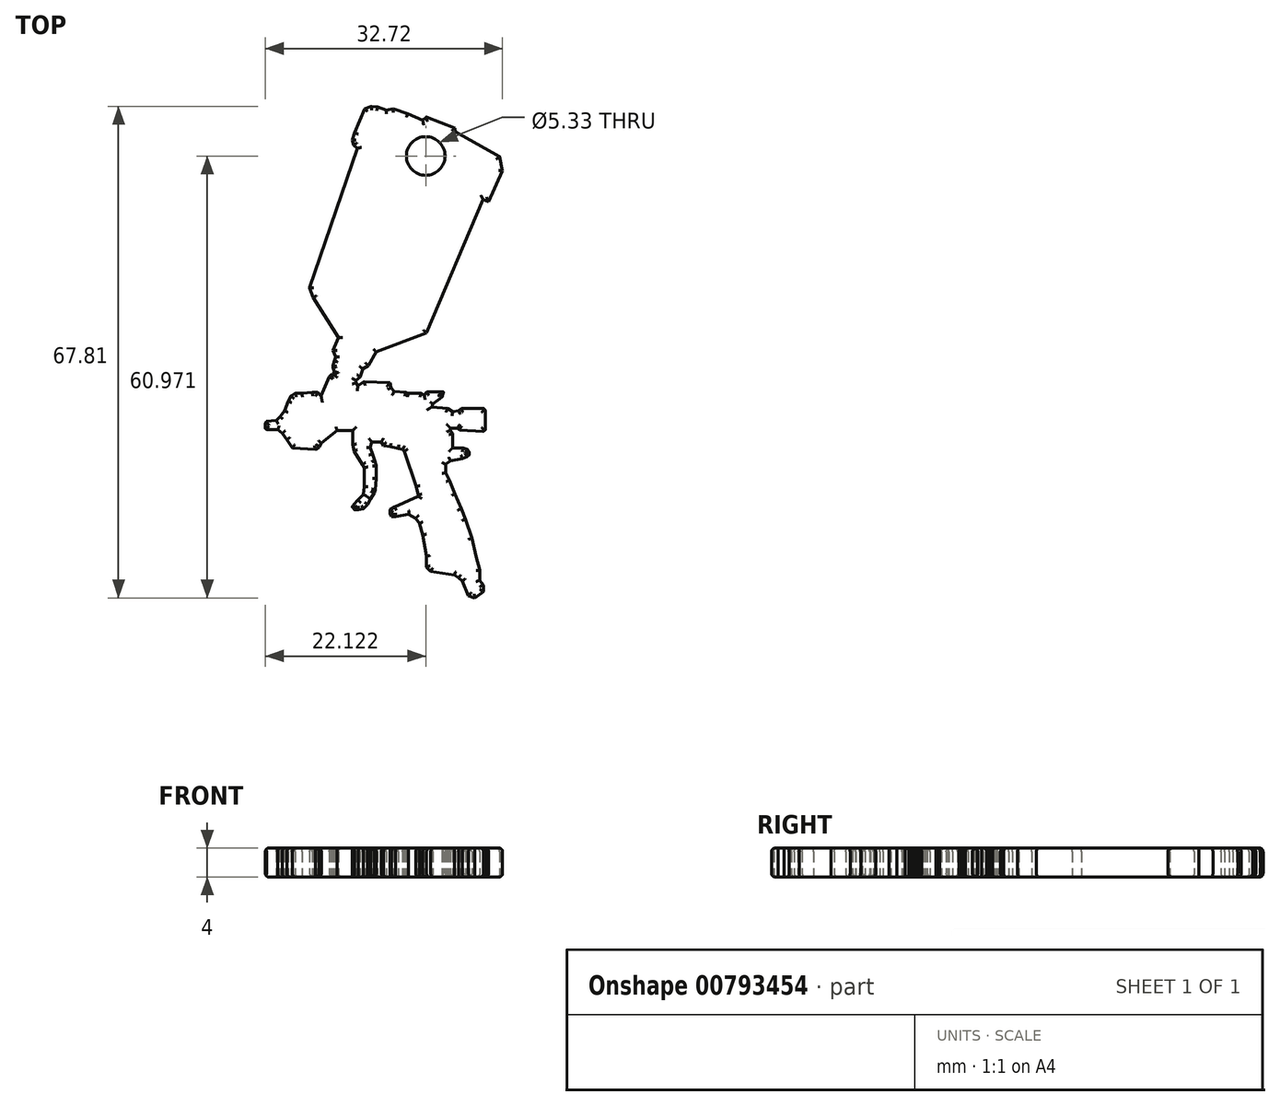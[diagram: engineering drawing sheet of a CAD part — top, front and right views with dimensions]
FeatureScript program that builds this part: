
annotation { "Feature Type Name" : "Feature", "Feature Type Description" : "" }
export const myFeature = defineFeature(function(context is Context, id is Id, definition is map)
    precondition{}
    {
        {
            var Q0;
            Q0=qCreatedBy(makeId("Top.planeOp"),FACE);
            var sketch = newSketch(context, id + "F0", { "sketchPlane" : qUnion([Q0])});
            skLineSegment(sketch, "E0", {"start": v(9.1, -28.8) * mm, "end": v(8.24, -26.79) * mm});
            skLineSegment(sketch, "E1", {"start": v(8.24, -26.79) * mm, "end": v(7.71, -26.36) * mm});
            skLineSegment(sketch, "E2", {"start": v(7.71, -26.36) * mm, "end": v(7.14, -25.97) * mm});
            skLineSegment(sketch, "E3", {"start": v(7.14, -25.97) * mm, "end": v(3.9, -25.45) * mm});
            skLineSegment(sketch, "E4", {"start": v(3.9, -25.45) * mm, "end": v(3.32, -24.88) * mm});
            skLineSegment(sketch, "E5", {"start": v(3.32, -24.88) * mm, "end": v(3.32, -23.3) * mm});
            skLineSegment(sketch, "E6", {"start": v(3.32, -23.3) * mm, "end": v(2.8, -20.43) * mm});
            skLineSegment(sketch, "E7", {"start": v(2.8, -20.43) * mm, "end": v(2.31, -18.85) * mm});
            skLineSegment(sketch, "E8", {"start": v(2.31, -18.85) * mm, "end": v(1.83, -18.13) * mm});
            skLineSegment(sketch, "E9", {"start": v(1.83, -18.13) * mm, "end": v(0.83, -17.56) * mm});
            skLineSegment(sketch, "E10", {"start": v(0.83, -17.56) * mm, "end": v(-0.93, -17.88) * mm});
            skLineSegment(sketch, "E11", {"start": v(-0.93, -17.88) * mm, "end": v(-1.5, -17.88) * mm});
            skLineSegment(sketch, "E12", {"start": v(-1.5, -17.88) * mm, "end": v(-1.75, -17.5) * mm});
            skLineSegment(sketch, "E13", {"start": v(-1.75, -17.5) * mm, "end": v(-1.75, -16.95) * mm});
            skLineSegment(sketch, "E14", {"start": v(-1.75, -16.95) * mm, "end": v(-1.07, -16.57) * mm});
            skLineSegment(sketch, "E15", {"start": v(-1.07, -16.57) * mm, "end": v(2.14, -15.08) * mm});
            skLineSegment(sketch, "E16", {"start": v(2.14, -15.08) * mm, "end": v(2.14, -14.85) * mm});
            skLineSegment(sketch, "E17", {"start": v(2.14, -14.85) * mm, "end": v(1.92, -13.74) * mm});
            skLineSegment(sketch, "E18", {"start": v(1.92, -13.74) * mm, "end": v(0.26, -8.88) * mm});
            skLineSegment(sketch, "E19", {"start": v(0.26, -8.88) * mm, "end": v(0, -8.63) * mm});
            skLineSegment(sketch, "E20", {"start": v(0, -8.63) * mm, "end": v(-0.6, -8.48) * mm});
            skLineSegment(sketch, "E21", {"start": v(-0.6, -8.48) * mm, "end": v(-1.68, -8.26) * mm});
            skLineSegment(sketch, "E22", {"start": v(-1.68, -8.26) * mm, "end": v(-2.6, -8.1) * mm});
            skLineSegment(sketch, "E23", {"start": v(-2.6, -8.1) * mm, "end": v(-2.92, -7.6) * mm});
            skLineSegment(sketch, "E24", {"start": v(-2.92, -7.6) * mm, "end": v(-4.24, -7.6) * mm});
            skLineSegment(sketch, "E25", {"start": v(-4.24, -7.6) * mm, "end": v(-4.43, -8.36) * mm});
            skLineSegment(sketch, "E26", {"start": v(-4.43, -8.36) * mm, "end": v(-4.14, -9.23) * mm});
            skLineSegment(sketch, "E27", {"start": v(-4.14, -9.23) * mm, "end": v(-3.79, -10.18) * mm});
            skLineSegment(sketch, "E28", {"start": v(-3.79, -10.18) * mm, "end": v(-3.65, -10.87) * mm});
            skLineSegment(sketch, "E29", {"start": v(-3.65, -10.87) * mm, "end": v(-3.65, -12.63) * mm});
            skLineSegment(sketch, "E30", {"start": v(-3.65, -12.63) * mm, "end": v(-3.78, -14.18) * mm});
            skLineSegment(sketch, "E31", {"start": v(-3.78, -14.18) * mm, "end": v(-3.9, -14.6) * mm});
            skLineSegment(sketch, "E32", {"start": v(-3.9, -14.6) * mm, "end": v(-4.38, -15.44) * mm});
            skLineSegment(sketch, "E33", {"start": v(-4.38, -15.44) * mm, "end": v(-4.81, -16.21) * mm});
            skLineSegment(sketch, "E34", {"start": v(-4.81, -16.21) * mm, "end": v(-5.4, -16.82) * mm});
            skLineSegment(sketch, "E35", {"start": v(-5.4, -16.82) * mm, "end": v(-6.07, -16.95) * mm});
            skLineSegment(sketch, "E36", {"start": v(-6.07, -16.95) * mm, "end": v(-6.62, -16.95) * mm});
            skLineSegment(sketch, "E37", {"start": v(-6.62, -16.95) * mm, "end": v(-6.94, -16.57) * mm});
            skLineSegment(sketch, "E38", {"start": v(-6.94, -16.57) * mm, "end": v(-6.74, -16.21) * mm});
            skLineSegment(sketch, "E39", {"start": v(-6.74, -16.21) * mm, "end": v(-6.14, -15.6) * mm});
            skLineSegment(sketch, "E40", {"start": v(-6.14, -15.6) * mm, "end": v(-5.38, -14.85) * mm});
            skLineSegment(sketch, "E41", {"start": v(-5.38, -14.85) * mm, "end": v(-5.26, -13.74) * mm});
            skLineSegment(sketch, "E42", {"start": v(-5.26, -13.74) * mm, "end": v(-5.26, -12.38) * mm});
            skLineSegment(sketch, "E43", {"start": v(-5.26, -12.38) * mm, "end": v(-5.26, -11.15) * mm});
            skLineSegment(sketch, "E44", {"start": v(-5.26, -11.15) * mm, "end": v(-5.5, -10.69) * mm});
            skLineSegment(sketch, "E45", {"start": v(-5.5, -10.69) * mm, "end": v(-6.7, -8.85) * mm});
            skLineSegment(sketch, "E46", {"start": v(-6.7, -8.85) * mm, "end": v(-6.87, -7.93) * mm});
            skLineSegment(sketch, "E47", {"start": v(-6.87, -7.93) * mm, "end": v(-6.87, -6.03) * mm});
            skLineSegment(sketch, "E48", {"start": v(-6.87, -6.03) * mm, "end": v(-9, -6.03) * mm});
            skLineSegment(sketch, "E49", {"start": v(-9, -6.03) * mm, "end": v(-11.2, -7.74) * mm});
            skLineSegment(sketch, "E50", {"start": v(-11.2, -7.74) * mm, "end": v(-11.5, -8.29) * mm});
            skLineSegment(sketch, "E51", {"start": v(-11.5, -8.29) * mm, "end": v(-12.01, -8.63) * mm});
            skLineSegment(sketch, "E52", {"start": v(-12.01, -8.63) * mm, "end": v(-15.17, -8.45) * mm});
            skLineSegment(sketch, "E53", {"start": v(-15.17, -8.45) * mm, "end": v(-15.95, -7.27) * mm});
            skLineSegment(sketch, "E54", {"start": v(-15.95, -7.27) * mm, "end": v(-16.58, -6.4) * mm});
            skLineSegment(sketch, "E55", {"start": v(-16.58, -6.4) * mm, "end": v(-17.2, -5.88) * mm});
            skLineSegment(sketch, "E56", {"start": v(-17.2, -5.88) * mm, "end": v(-18.72, -5.88) * mm});
            skLineSegment(sketch, "E57", {"start": v(-18.72, -5.88) * mm, "end": v(-18.92, -5.77) * mm});
            skLineSegment(sketch, "E58", {"start": v(-18.92, -5.77) * mm, "end": v(-18.92, -5.02) * mm});
            skLineSegment(sketch, "E59", {"start": v(-18.92, -5.02) * mm, "end": v(-18.78, -4.77) * mm});
            skLineSegment(sketch, "E60", {"start": v(-18.78, -4.77) * mm, "end": v(-17.4, -4.62) * mm});
            skLineSegment(sketch, "E61", {"start": v(-17.4, -4.62) * mm, "end": v(-16.88, -4.11) * mm});
            skLineSegment(sketch, "E62", {"start": v(-16.88, -4.11) * mm, "end": v(-16.3, -3.27) * mm});
            skLineSegment(sketch, "E63", {"start": v(-16.3, -3.27) * mm, "end": v(-15.78, -1.95) * mm});
            skLineSegment(sketch, "E64", {"start": v(-15.78, -1.95) * mm, "end": v(-15.38, -1.22) * mm});
            skLineSegment(sketch, "E65", {"start": v(-15.38, -1.22) * mm, "end": v(-14.79, -0.87) * mm});
            skLineSegment(sketch, "E66", {"start": v(-14.79, -0.87) * mm, "end": v(-13.83, -0.87) * mm});
            skLineSegment(sketch, "E67", {"start": v(-13.83, -0.87) * mm, "end": v(-12.43, -0.75) * mm});
            skLineSegment(sketch, "E68", {"start": v(-12.43, -0.75) * mm, "end": v(-11.72, -0.75) * mm});
            skLineSegment(sketch, "E69", {"start": v(-11.72, -0.75) * mm, "end": v(-11.23, -1.26) * mm});
            skLineSegment(sketch, "E70", {"start": v(-11.23, -1.26) * mm, "end": v(-10.1, 1.4) * mm});
            skLineSegment(sketch, "E71", {"start": v(-10.1, 1.4) * mm, "end": v(-9.85, 1.65) * mm});
            skLineSegment(sketch, "E72", {"start": v(-9.85, 1.65) * mm, "end": v(-9.56, 1.7) * mm});
            skLineSegment(sketch, "E73", {"start": v(-9.56, 1.7) * mm, "end": v(-9.6, 1.88) * mm});
            skLineSegment(sketch, "E74", {"start": v(-9.6, 1.88) * mm, "end": v(-9.39, 2.08) * mm});
            skLineSegment(sketch, "E75", {"start": v(-9.39, 2.08) * mm, "end": v(-9.61, 2.7) * mm});
            skLineSegment(sketch, "E76", {"start": v(-9.61, 2.7) * mm, "end": v(-9.61, 2.93) * mm});
            skLineSegment(sketch, "E77", {"start": v(-9.61, 2.93) * mm, "end": v(-9.4, 3.6) * mm});
            skLineSegment(sketch, "E78", {"start": v(-9.4, 3.6) * mm, "end": v(-9.23, 4.13) * mm});
            skLineSegment(sketch, "E79", {"start": v(-9.23, 4.13) * mm, "end": v(-9.56, 5.02) * mm});
            skLineSegment(sketch, "E80", {"start": v(-9.56, 5.02) * mm, "end": v(-8.84, 6.8) * mm});
            skLineSegment(sketch, "E81", {"start": v(-8.84, 6.8) * mm, "end": v(-12.32, 12.35) * mm});
            skLineSegment(sketch, "E82", {"start": v(-12.32, 12.35) * mm, "end": v(-12.8, 13.65) * mm});
            skLineSegment(sketch, "E83", {"start": v(-12.8, 13.65) * mm, "end": v(-6.26, 32.91) * mm});
            skLineSegment(sketch, "E84", {"start": v(-6.26, 32.91) * mm, "end": v(-6.7, 33.38) * mm});
            skLineSegment(sketch, "E85", {"start": v(-6.7, 33.38) * mm, "end": v(-6.94, 34.03) * mm});
            skLineSegment(sketch, "E86", {"start": v(-6.94, 34.03) * mm, "end": v(-6.6, 35.06) * mm});
            skLineSegment(sketch, "E87", {"start": v(-6.6, 35.06) * mm, "end": v(-5.2, 38.37) * mm});
            skLineSegment(sketch, "E88", {"start": v(-5.2, 38.37) * mm, "end": v(-4.32, 38.7) * mm});
            skLineSegment(sketch, "E89", {"start": v(-4.32, 38.7) * mm, "end": v(-3.45, 38.6) * mm});
            skLineSegment(sketch, "E90", {"start": v(-3.45, 38.6) * mm, "end": v(-2.2, 38.18) * mm});
            skLineSegment(sketch, "E91", {"start": v(-2.2, 38.18) * mm, "end": v(-1.25, 38.36) * mm});
            skLineSegment(sketch, "E92", {"start": v(-1.25, 38.36) * mm, "end": v(0.73, 37.69) * mm});
            skLineSegment(sketch, "E93", {"start": v(0.73, 37.69) * mm, "end": v(2.8, 36.77) * mm});
            skLineSegment(sketch, "E94", {"start": v(2.8, 36.77) * mm, "end": v(3.29, 37.25) * mm});
            skLineSegment(sketch, "E95", {"start": v(3.29, 37.25) * mm, "end": v(7.21, 35.67) * mm});
            skLineSegment(sketch, "E96", {"start": v(7.21, 35.67) * mm, "end": v(7.3, 35.2) * mm});
            skLineSegment(sketch, "E97", {"start": v(7.3, 35.2) * mm, "end": v(13.42, 31.78) * mm});
            skLineSegment(sketch, "E98", {"start": v(13.42, 31.78) * mm, "end": v(13.8, 29.8) * mm});
            skLineSegment(sketch, "E99", {"start": v(13.8, 29.8) * mm, "end": v(11.86, 25.58) * mm});
            skLineSegment(sketch, "E100", {"start": v(11.86, 25.58) * mm, "end": v(11.1, 25.83) * mm});
            skLineSegment(sketch, "E101", {"start": v(11.1, 25.83) * mm, "end": v(3.29, 7.42) * mm});
            skLineSegment(sketch, "E102", {"start": v(3.29, 7.42) * mm, "end": v(-1.5, 5.63) * mm});
            skLineSegment(sketch, "E103", {"start": v(-1.5, 5.63) * mm, "end": v(-3.65, 4.82) * mm});
            skLineSegment(sketch, "E104", {"start": v(-3.65, 4.82) * mm, "end": v(-4.71, 2.93) * mm});
            skLineSegment(sketch, "E105", {"start": v(-4.71, 2.93) * mm, "end": v(-5.5, 2.5) * mm});
            skLineSegment(sketch, "E106", {"start": v(-5.5, 2.5) * mm, "end": v(-5.83, 1.38) * mm});
            skLineSegment(sketch, "E107", {"start": v(-5.83, 1.38) * mm, "end": v(-6.44, 0.93) * mm});
            skLineSegment(sketch, "E108", {"start": v(-6.44, 0.93) * mm, "end": v(-6.44, 0.56) * mm});
            skLineSegment(sketch, "E109", {"start": v(-6.44, 0.56) * mm, "end": v(-6.15, 0.15) * mm});
            skLineSegment(sketch, "E110", {"start": v(-6.15, 0.15) * mm, "end": v(-5.32, 0.75) * mm});
            skLineSegment(sketch, "E111", {"start": v(-5.32, 0.75) * mm, "end": v(-1.74, 0.56) * mm});
            skLineSegment(sketch, "E112", {"start": v(-1.74, 0.56) * mm, "end": v(-1.58, -0.12) * mm});
            skLineSegment(sketch, "E113", {"start": v(-1.58, -0.12) * mm, "end": v(-1.17, -0.65) * mm});
            skLineSegment(sketch, "E114", {"start": v(-1.17, -0.65) * mm, "end": v(0.41, -0.77) * mm});
            skLineSegment(sketch, "E115", {"start": v(0.41, -0.77) * mm, "end": v(0.77, -0.86) * mm});
            skLineSegment(sketch, "E116", {"start": v(0.77, -0.86) * mm, "end": v(2.55, -0.86) * mm});
            skLineSegment(sketch, "E117", {"start": v(2.55, -0.86) * mm, "end": v(3, -1.11) * mm});
            skLineSegment(sketch, "E118", {"start": v(3, -1.11) * mm, "end": v(3.39, -0.7) * mm});
            skLineSegment(sketch, "E119", {"start": v(3.39, -0.7) * mm, "end": v(5.67, -0.7) * mm});
            skLineSegment(sketch, "E120", {"start": v(5.67, -0.7) * mm, "end": v(5.46, -1.4) * mm});
            skLineSegment(sketch, "E121", {"start": v(5.46, -1.4) * mm, "end": v(4.9, -1.83) * mm});
            skLineSegment(sketch, "E122", {"start": v(4.9, -1.83) * mm, "end": v(4.2, -2.36) * mm});
            skLineSegment(sketch, "E123", {"start": v(4.2, -2.36) * mm, "end": v(4.05, -2.76) * mm});
            skLineSegment(sketch, "E124", {"start": v(4.05, -2.76) * mm, "end": v(6.2, -2.96) * mm});
            skLineSegment(sketch, "E125", {"start": v(6.2, -2.96) * mm, "end": v(6.92, -3.44) * mm});
            skLineSegment(sketch, "E126", {"start": v(6.92, -3.44) * mm, "end": v(7.73, -3.28) * mm});
            skLineSegment(sketch, "E127", {"start": v(7.73, -3.28) * mm, "end": v(8.12, -2.98) * mm});
            skLineSegment(sketch, "E128", {"start": v(8.12, -2.98) * mm, "end": v(11.23, -2.98) * mm});
            skLineSegment(sketch, "E129", {"start": v(11.23, -2.98) * mm, "end": v(11.44, -3.27) * mm});
            skLineSegment(sketch, "E130", {"start": v(11.44, -3.27) * mm, "end": v(11.44, -5.91) * mm});
            skLineSegment(sketch, "E131", {"start": v(11.44, -5.91) * mm, "end": v(11.14, -6.14) * mm});
            skLineSegment(sketch, "E132", {"start": v(11.14, -6.14) * mm, "end": v(7.85, -5.95) * mm});
            skLineSegment(sketch, "E133", {"start": v(7.85, -5.95) * mm, "end": v(7.64, -5.68) * mm});
            skLineSegment(sketch, "E134", {"start": v(7.64, -5.68) * mm, "end": v(6.6, -5.68) * mm});
            skLineSegment(sketch, "E135", {"start": v(6.6, -5.68) * mm, "end": v(6.6, -6.01) * mm});
            skLineSegment(sketch, "E136", {"start": v(6.6, -6.01) * mm, "end": v(6.91, -6.42) * mm});
            skLineSegment(sketch, "E137", {"start": v(6.91, -6.42) * mm, "end": v(6.91, -8.4) * mm});
            skLineSegment(sketch, "E138", {"start": v(6.91, -8.4) * mm, "end": v(8.35, -8.4) * mm});
            skLineSegment(sketch, "E139", {"start": v(8.35, -8.4) * mm, "end": v(8.94, -8.62) * mm});
            skLineSegment(sketch, "E140", {"start": v(8.94, -8.62) * mm, "end": v(9.21, -8.98) * mm});
            skLineSegment(sketch, "E141", {"start": v(9.21, -8.98) * mm, "end": v(9.21, -9.35) * mm});
            skLineSegment(sketch, "E142", {"start": v(9.21, -9.35) * mm, "end": v(8.88, -9.6) * mm});
            skLineSegment(sketch, "E143", {"start": v(8.88, -9.6) * mm, "end": v(8.23, -9.87) * mm});
            skLineSegment(sketch, "E144", {"start": v(8.23, -9.87) * mm, "end": v(6.6, -10.2) * mm});
            skLineSegment(sketch, "E145", {"start": v(6.6, -10.2) * mm, "end": v(5.97, -10.67) * mm});
            skLineSegment(sketch, "E146", {"start": v(5.97, -10.67) * mm, "end": v(5.97, -11.26) * mm});
            skLineSegment(sketch, "E147", {"start": v(5.97, -11.26) * mm, "end": v(5.97, -11.83) * mm});
            skLineSegment(sketch, "E148", {"start": v(5.97, -11.83) * mm, "end": v(6.47, -12.87) * mm});
            skLineSegment(sketch, "E149", {"start": v(6.47, -12.87) * mm, "end": v(7.23, -14.77) * mm});
            skLineSegment(sketch, "E150", {"start": v(7.23, -14.77) * mm, "end": v(8.1, -16.8) * mm});
            skLineSegment(sketch, "E151", {"start": v(8.1, -16.8) * mm, "end": v(8.66, -18.26) * mm});
            skLineSegment(sketch, "E152", {"start": v(8.66, -18.26) * mm, "end": v(9.55, -20.9) * mm});
            skLineSegment(sketch, "E153", {"start": v(9.55, -20.9) * mm, "end": v(10.18, -23.41) * mm});
            skLineSegment(sketch, "E154", {"start": v(10.18, -23.41) * mm, "end": v(10.65, -25.27) * mm});
            skLineSegment(sketch, "E155", {"start": v(10.65, -25.27) * mm, "end": v(10.65, -26.16) * mm});
            skLineSegment(sketch, "E156", {"start": v(10.65, -26.16) * mm, "end": v(10.65, -26.69) * mm});
            skLineSegment(sketch, "E157", {"start": v(10.65, -26.69) * mm, "end": v(11.16, -27.35) * mm});
            skLineSegment(sketch, "E158", {"start": v(11.16, -27.35) * mm, "end": v(11.16, -28.21) * mm});
            skLineSegment(sketch, "E159", {"start": v(11.16, -28.21) * mm, "end": v(10.6, -28.65) * mm});
            skLineSegment(sketch, "E160", {"start": v(10.6, -28.65) * mm, "end": v(9.99, -29.11) * mm});
            skLineSegment(sketch, "E161", {"start": v(9.99, -29.11) * mm, "end": v(9.1, -28.8) * mm});
            skCircle(sketch, "E162", {"center": v(3.2, 31.86) * mm, "radius": 2.67 * mm});
            skSolve(sketch);
        }
        {
            var Q0;
            Q0 = qSketchRegion(id + "F0", true);
            var Q1;
            Q1=makeQuery(id+"F0.imprint","IMPRINT",FACE,{"disambiguationData":[TD([[makeQuery(id+"F0.imprint","IMPRINT",EDGE,{"derivedFrom":sQuery(id+"F0.wireOp",EDGE,"E0")}),-1.0]])]});
            extrude(context, id + "F1", {"entities" : qUnion([Q0, Q1]), "depth" : 4 * mm, "offsetDistance" : 25 * mm});
        }
        {
            var Q0;
            Q0=makeQuery(id+"F1.opExtrude","CAP_FACE",FACE,{"disambiguationData":[OSD([sQuery(id+"F0.wireOp",EDGE,"E0"),sQuery(id+"F0.wireOp",EDGE,"E1"),sQuery(id+"F0.wireOp",EDGE,"E2"),sQuery(id+"F0.wireOp",EDGE,"E3"),sQuery(id+"F0.wireOp",EDGE,"E4"),sQuery(id+"F0.wireOp",EDGE,"E5"),sQuery(id+"F0.wireOp",EDGE,"E6"),sQuery(id+"F0.wireOp",EDGE,"E7"),sQuery(id+"F0.wireOp",EDGE,"E8"),sQuery(id+"F0.wireOp",EDGE,"E9"),sQuery(id+"F0.wireOp",EDGE,"E10"),sQuery(id+"F0.wireOp",EDGE,"E11"),sQuery(id+"F0.wireOp",EDGE,"E12"),sQuery(id+"F0.wireOp",EDGE,"E13"),sQuery(id+"F0.wireOp",EDGE,"E14"),sQuery(id+"F0.wireOp",EDGE,"E15"),sQuery(id+"F0.wireOp",EDGE,"E16"),sQuery(id+"F0.wireOp",EDGE,"E17"),sQuery(id+"F0.wireOp",EDGE,"E18"),sQuery(id+"F0.wireOp",EDGE,"E19"),sQuery(id+"F0.wireOp",EDGE,"E20"),sQuery(id+"F0.wireOp",EDGE,"E21"),sQuery(id+"F0.wireOp",EDGE,"E22"),sQuery(id+"F0.wireOp",EDGE,"E23"),sQuery(id+"F0.wireOp",EDGE,"E24"),sQuery(id+"F0.wireOp",EDGE,"E25"),sQuery(id+"F0.wireOp",EDGE,"E26"),sQuery(id+"F0.wireOp",EDGE,"E27"),sQuery(id+"F0.wireOp",EDGE,"E28"),sQuery(id+"F0.wireOp",EDGE,"E29"),sQuery(id+"F0.wireOp",EDGE,"E30"),sQuery(id+"F0.wireOp",EDGE,"E31"),sQuery(id+"F0.wireOp",EDGE,"E32"),sQuery(id+"F0.wireOp",EDGE,"E33"),sQuery(id+"F0.wireOp",EDGE,"E34"),sQuery(id+"F0.wireOp",EDGE,"E35"),sQuery(id+"F0.wireOp",EDGE,"E36"),sQuery(id+"F0.wireOp",EDGE,"E37"),sQuery(id+"F0.wireOp",EDGE,"E38"),sQuery(id+"F0.wireOp",EDGE,"E39"),sQuery(id+"F0.wireOp",EDGE,"E40"),sQuery(id+"F0.wireOp",EDGE,"E41"),sQuery(id+"F0.wireOp",EDGE,"E42"),sQuery(id+"F0.wireOp",EDGE,"E43"),sQuery(id+"F0.wireOp",EDGE,"E44"),sQuery(id+"F0.wireOp",EDGE,"E45"),sQuery(id+"F0.wireOp",EDGE,"E46"),sQuery(id+"F0.wireOp",EDGE,"E47"),sQuery(id+"F0.wireOp",EDGE,"E48"),sQuery(id+"F0.wireOp",EDGE,"E49"),sQuery(id+"F0.wireOp",EDGE,"E50"),sQuery(id+"F0.wireOp",EDGE,"E51"),sQuery(id+"F0.wireOp",EDGE,"E52"),sQuery(id+"F0.wireOp",EDGE,"E53"),sQuery(id+"F0.wireOp",EDGE,"E54"),sQuery(id+"F0.wireOp",EDGE,"E55"),sQuery(id+"F0.wireOp",EDGE,"E56"),sQuery(id+"F0.wireOp",EDGE,"E57"),sQuery(id+"F0.wireOp",EDGE,"E58"),sQuery(id+"F0.wireOp",EDGE,"E59"),sQuery(id+"F0.wireOp",EDGE,"E60"),sQuery(id+"F0.wireOp",EDGE,"E61"),sQuery(id+"F0.wireOp",EDGE,"E62"),sQuery(id+"F0.wireOp",EDGE,"E63"),sQuery(id+"F0.wireOp",EDGE,"E64"),sQuery(id+"F0.wireOp",EDGE,"E65"),sQuery(id+"F0.wireOp",EDGE,"E66"),sQuery(id+"F0.wireOp",EDGE,"E67"),sQuery(id+"F0.wireOp",EDGE,"E68"),sQuery(id+"F0.wireOp",EDGE,"E69"),sQuery(id+"F0.wireOp",EDGE,"E70"),sQuery(id+"F0.wireOp",EDGE,"E71"),sQuery(id+"F0.wireOp",EDGE,"E72"),sQuery(id+"F0.wireOp",EDGE,"E73"),sQuery(id+"F0.wireOp",EDGE,"E74"),sQuery(id+"F0.wireOp",EDGE,"E75"),sQuery(id+"F0.wireOp",EDGE,"E76"),sQuery(id+"F0.wireOp",EDGE,"E77"),sQuery(id+"F0.wireOp",EDGE,"E78"),sQuery(id+"F0.wireOp",EDGE,"E79"),sQuery(id+"F0.wireOp",EDGE,"E80"),sQuery(id+"F0.wireOp",EDGE,"E81"),sQuery(id+"F0.wireOp",EDGE,"E82"),sQuery(id+"F0.wireOp",EDGE,"E83"),sQuery(id+"F0.wireOp",EDGE,"E84"),sQuery(id+"F0.wireOp",EDGE,"E85"),sQuery(id+"F0.wireOp",EDGE,"E86"),sQuery(id+"F0.wireOp",EDGE,"E87"),sQuery(id+"F0.wireOp",EDGE,"E88"),sQuery(id+"F0.wireOp",EDGE,"E89"),sQuery(id+"F0.wireOp",EDGE,"E90"),sQuery(id+"F0.wireOp",EDGE,"E91"),sQuery(id+"F0.wireOp",EDGE,"E92"),sQuery(id+"F0.wireOp",EDGE,"E93"),sQuery(id+"F0.wireOp",EDGE,"E94"),sQuery(id+"F0.wireOp",EDGE,"E95"),sQuery(id+"F0.wireOp",EDGE,"E96"),sQuery(id+"F0.wireOp",EDGE,"E97"),sQuery(id+"F0.wireOp",EDGE,"E98"),sQuery(id+"F0.wireOp",EDGE,"E99"),sQuery(id+"F0.wireOp",EDGE,"E100"),sQuery(id+"F0.wireOp",EDGE,"E101"),sQuery(id+"F0.wireOp",EDGE,"E102"),sQuery(id+"F0.wireOp",EDGE,"E103"),sQuery(id+"F0.wireOp",EDGE,"E104"),sQuery(id+"F0.wireOp",EDGE,"E105"),sQuery(id+"F0.wireOp",EDGE,"E106"),sQuery(id+"F0.wireOp",EDGE,"E107"),sQuery(id+"F0.wireOp",EDGE,"E108"),sQuery(id+"F0.wireOp",EDGE,"E109"),sQuery(id+"F0.wireOp",EDGE,"E110"),sQuery(id+"F0.wireOp",EDGE,"E111"),sQuery(id+"F0.wireOp",EDGE,"E112"),sQuery(id+"F0.wireOp",EDGE,"E113"),sQuery(id+"F0.wireOp",EDGE,"E114"),sQuery(id+"F0.wireOp",EDGE,"E115"),sQuery(id+"F0.wireOp",EDGE,"E116"),sQuery(id+"F0.wireOp",EDGE,"E117"),sQuery(id+"F0.wireOp",EDGE,"E118"),sQuery(id+"F0.wireOp",EDGE,"E119"),sQuery(id+"F0.wireOp",EDGE,"E120"),sQuery(id+"F0.wireOp",EDGE,"E121"),sQuery(id+"F0.wireOp",EDGE,"E122"),sQuery(id+"F0.wireOp",EDGE,"E123"),sQuery(id+"F0.wireOp",EDGE,"E124"),sQuery(id+"F0.wireOp",EDGE,"E125"),sQuery(id+"F0.wireOp",EDGE,"E126"),sQuery(id+"F0.wireOp",EDGE,"E127"),sQuery(id+"F0.wireOp",EDGE,"E128"),sQuery(id+"F0.wireOp",EDGE,"E129"),sQuery(id+"F0.wireOp",EDGE,"E130"),sQuery(id+"F0.wireOp",EDGE,"E131"),sQuery(id+"F0.wireOp",EDGE,"E132"),sQuery(id+"F0.wireOp",EDGE,"E133"),sQuery(id+"F0.wireOp",EDGE,"E134"),sQuery(id+"F0.wireOp",EDGE,"E135"),sQuery(id+"F0.wireOp",EDGE,"E136"),sQuery(id+"F0.wireOp",EDGE,"E137"),sQuery(id+"F0.wireOp",EDGE,"E138"),sQuery(id+"F0.wireOp",EDGE,"E139"),sQuery(id+"F0.wireOp",EDGE,"E140"),sQuery(id+"F0.wireOp",EDGE,"E141"),sQuery(id+"F0.wireOp",EDGE,"E142"),sQuery(id+"F0.wireOp",EDGE,"E143"),sQuery(id+"F0.wireOp",EDGE,"E144"),sQuery(id+"F0.wireOp",EDGE,"E145"),sQuery(id+"F0.wireOp",EDGE,"E146"),sQuery(id+"F0.wireOp",EDGE,"E147"),sQuery(id+"F0.wireOp",EDGE,"E148"),sQuery(id+"F0.wireOp",EDGE,"E149"),sQuery(id+"F0.wireOp",EDGE,"E150"),sQuery(id+"F0.wireOp",EDGE,"E151"),sQuery(id+"F0.wireOp",EDGE,"E152"),sQuery(id+"F0.wireOp",EDGE,"E153"),sQuery(id+"F0.wireOp",EDGE,"E154"),sQuery(id+"F0.wireOp",EDGE,"E155"),sQuery(id+"F0.wireOp",EDGE,"E156"),sQuery(id+"F0.wireOp",EDGE,"E157"),sQuery(id+"F0.wireOp",EDGE,"E158"),sQuery(id+"F0.wireOp",EDGE,"E159"),sQuery(id+"F0.wireOp",EDGE,"E160"),sQuery(id+"F0.wireOp",EDGE,"E161"),sQuery(id+"F0.wireOp",EDGE,"E162")])],"isStart":false});
            var Q1;
            Q1=makeQuery(id+"F1.opExtrude","CAP_FACE",FACE,{"disambiguationData":[OSD([sQuery(id+"F0.wireOp",EDGE,"E0"),sQuery(id+"F0.wireOp",EDGE,"E1"),sQuery(id+"F0.wireOp",EDGE,"E2"),sQuery(id+"F0.wireOp",EDGE,"E3"),sQuery(id+"F0.wireOp",EDGE,"E4"),sQuery(id+"F0.wireOp",EDGE,"E5"),sQuery(id+"F0.wireOp",EDGE,"E6"),sQuery(id+"F0.wireOp",EDGE,"E7"),sQuery(id+"F0.wireOp",EDGE,"E8"),sQuery(id+"F0.wireOp",EDGE,"E9"),sQuery(id+"F0.wireOp",EDGE,"E10"),sQuery(id+"F0.wireOp",EDGE,"E11"),sQuery(id+"F0.wireOp",EDGE,"E12"),sQuery(id+"F0.wireOp",EDGE,"E13"),sQuery(id+"F0.wireOp",EDGE,"E14"),sQuery(id+"F0.wireOp",EDGE,"E15"),sQuery(id+"F0.wireOp",EDGE,"E16"),sQuery(id+"F0.wireOp",EDGE,"E17"),sQuery(id+"F0.wireOp",EDGE,"E18"),sQuery(id+"F0.wireOp",EDGE,"E19"),sQuery(id+"F0.wireOp",EDGE,"E20"),sQuery(id+"F0.wireOp",EDGE,"E21"),sQuery(id+"F0.wireOp",EDGE,"E22"),sQuery(id+"F0.wireOp",EDGE,"E23"),sQuery(id+"F0.wireOp",EDGE,"E24"),sQuery(id+"F0.wireOp",EDGE,"E25"),sQuery(id+"F0.wireOp",EDGE,"E26"),sQuery(id+"F0.wireOp",EDGE,"E27"),sQuery(id+"F0.wireOp",EDGE,"E28"),sQuery(id+"F0.wireOp",EDGE,"E29"),sQuery(id+"F0.wireOp",EDGE,"E30"),sQuery(id+"F0.wireOp",EDGE,"E31"),sQuery(id+"F0.wireOp",EDGE,"E32"),sQuery(id+"F0.wireOp",EDGE,"E33"),sQuery(id+"F0.wireOp",EDGE,"E34"),sQuery(id+"F0.wireOp",EDGE,"E35"),sQuery(id+"F0.wireOp",EDGE,"E36"),sQuery(id+"F0.wireOp",EDGE,"E37"),sQuery(id+"F0.wireOp",EDGE,"E38"),sQuery(id+"F0.wireOp",EDGE,"E39"),sQuery(id+"F0.wireOp",EDGE,"E40"),sQuery(id+"F0.wireOp",EDGE,"E41"),sQuery(id+"F0.wireOp",EDGE,"E42"),sQuery(id+"F0.wireOp",EDGE,"E43"),sQuery(id+"F0.wireOp",EDGE,"E44"),sQuery(id+"F0.wireOp",EDGE,"E45"),sQuery(id+"F0.wireOp",EDGE,"E46"),sQuery(id+"F0.wireOp",EDGE,"E47"),sQuery(id+"F0.wireOp",EDGE,"E48"),sQuery(id+"F0.wireOp",EDGE,"E49"),sQuery(id+"F0.wireOp",EDGE,"E50"),sQuery(id+"F0.wireOp",EDGE,"E51"),sQuery(id+"F0.wireOp",EDGE,"E52"),sQuery(id+"F0.wireOp",EDGE,"E53"),sQuery(id+"F0.wireOp",EDGE,"E54"),sQuery(id+"F0.wireOp",EDGE,"E55"),sQuery(id+"F0.wireOp",EDGE,"E56"),sQuery(id+"F0.wireOp",EDGE,"E57"),sQuery(id+"F0.wireOp",EDGE,"E58"),sQuery(id+"F0.wireOp",EDGE,"E59"),sQuery(id+"F0.wireOp",EDGE,"E60"),sQuery(id+"F0.wireOp",EDGE,"E61"),sQuery(id+"F0.wireOp",EDGE,"E62"),sQuery(id+"F0.wireOp",EDGE,"E63"),sQuery(id+"F0.wireOp",EDGE,"E64"),sQuery(id+"F0.wireOp",EDGE,"E65"),sQuery(id+"F0.wireOp",EDGE,"E66"),sQuery(id+"F0.wireOp",EDGE,"E67"),sQuery(id+"F0.wireOp",EDGE,"E68"),sQuery(id+"F0.wireOp",EDGE,"E69"),sQuery(id+"F0.wireOp",EDGE,"E70"),sQuery(id+"F0.wireOp",EDGE,"E71"),sQuery(id+"F0.wireOp",EDGE,"E72"),sQuery(id+"F0.wireOp",EDGE,"E73"),sQuery(id+"F0.wireOp",EDGE,"E74"),sQuery(id+"F0.wireOp",EDGE,"E75"),sQuery(id+"F0.wireOp",EDGE,"E76"),sQuery(id+"F0.wireOp",EDGE,"E77"),sQuery(id+"F0.wireOp",EDGE,"E78"),sQuery(id+"F0.wireOp",EDGE,"E79"),sQuery(id+"F0.wireOp",EDGE,"E80"),sQuery(id+"F0.wireOp",EDGE,"E81"),sQuery(id+"F0.wireOp",EDGE,"E82"),sQuery(id+"F0.wireOp",EDGE,"E83"),sQuery(id+"F0.wireOp",EDGE,"E84"),sQuery(id+"F0.wireOp",EDGE,"E85"),sQuery(id+"F0.wireOp",EDGE,"E86"),sQuery(id+"F0.wireOp",EDGE,"E87"),sQuery(id+"F0.wireOp",EDGE,"E88"),sQuery(id+"F0.wireOp",EDGE,"E89"),sQuery(id+"F0.wireOp",EDGE,"E90"),sQuery(id+"F0.wireOp",EDGE,"E91"),sQuery(id+"F0.wireOp",EDGE,"E92"),sQuery(id+"F0.wireOp",EDGE,"E93"),sQuery(id+"F0.wireOp",EDGE,"E94"),sQuery(id+"F0.wireOp",EDGE,"E95"),sQuery(id+"F0.wireOp",EDGE,"E96"),sQuery(id+"F0.wireOp",EDGE,"E97"),sQuery(id+"F0.wireOp",EDGE,"E98"),sQuery(id+"F0.wireOp",EDGE,"E99"),sQuery(id+"F0.wireOp",EDGE,"E100"),sQuery(id+"F0.wireOp",EDGE,"E101"),sQuery(id+"F0.wireOp",EDGE,"E102"),sQuery(id+"F0.wireOp",EDGE,"E103"),sQuery(id+"F0.wireOp",EDGE,"E104"),sQuery(id+"F0.wireOp",EDGE,"E105"),sQuery(id+"F0.wireOp",EDGE,"E106"),sQuery(id+"F0.wireOp",EDGE,"E107"),sQuery(id+"F0.wireOp",EDGE,"E108"),sQuery(id+"F0.wireOp",EDGE,"E109"),sQuery(id+"F0.wireOp",EDGE,"E110"),sQuery(id+"F0.wireOp",EDGE,"E111"),sQuery(id+"F0.wireOp",EDGE,"E112"),sQuery(id+"F0.wireOp",EDGE,"E113"),sQuery(id+"F0.wireOp",EDGE,"E114"),sQuery(id+"F0.wireOp",EDGE,"E115"),sQuery(id+"F0.wireOp",EDGE,"E116"),sQuery(id+"F0.wireOp",EDGE,"E117"),sQuery(id+"F0.wireOp",EDGE,"E118"),sQuery(id+"F0.wireOp",EDGE,"E119"),sQuery(id+"F0.wireOp",EDGE,"E120"),sQuery(id+"F0.wireOp",EDGE,"E121"),sQuery(id+"F0.wireOp",EDGE,"E122"),sQuery(id+"F0.wireOp",EDGE,"E123"),sQuery(id+"F0.wireOp",EDGE,"E124"),sQuery(id+"F0.wireOp",EDGE,"E125"),sQuery(id+"F0.wireOp",EDGE,"E126"),sQuery(id+"F0.wireOp",EDGE,"E127"),sQuery(id+"F0.wireOp",EDGE,"E128"),sQuery(id+"F0.wireOp",EDGE,"E129"),sQuery(id+"F0.wireOp",EDGE,"E130"),sQuery(id+"F0.wireOp",EDGE,"E131"),sQuery(id+"F0.wireOp",EDGE,"E132"),sQuery(id+"F0.wireOp",EDGE,"E133"),sQuery(id+"F0.wireOp",EDGE,"E134"),sQuery(id+"F0.wireOp",EDGE,"E135"),sQuery(id+"F0.wireOp",EDGE,"E136"),sQuery(id+"F0.wireOp",EDGE,"E137"),sQuery(id+"F0.wireOp",EDGE,"E138"),sQuery(id+"F0.wireOp",EDGE,"E139"),sQuery(id+"F0.wireOp",EDGE,"E140"),sQuery(id+"F0.wireOp",EDGE,"E141"),sQuery(id+"F0.wireOp",EDGE,"E142"),sQuery(id+"F0.wireOp",EDGE,"E143"),sQuery(id+"F0.wireOp",EDGE,"E144"),sQuery(id+"F0.wireOp",EDGE,"E145"),sQuery(id+"F0.wireOp",EDGE,"E146"),sQuery(id+"F0.wireOp",EDGE,"E147"),sQuery(id+"F0.wireOp",EDGE,"E148"),sQuery(id+"F0.wireOp",EDGE,"E149"),sQuery(id+"F0.wireOp",EDGE,"E150"),sQuery(id+"F0.wireOp",EDGE,"E151"),sQuery(id+"F0.wireOp",EDGE,"E152"),sQuery(id+"F0.wireOp",EDGE,"E153"),sQuery(id+"F0.wireOp",EDGE,"E154"),sQuery(id+"F0.wireOp",EDGE,"E155"),sQuery(id+"F0.wireOp",EDGE,"E156"),sQuery(id+"F0.wireOp",EDGE,"E157"),sQuery(id+"F0.wireOp",EDGE,"E158"),sQuery(id+"F0.wireOp",EDGE,"E159"),sQuery(id+"F0.wireOp",EDGE,"E160"),sQuery(id+"F0.wireOp",EDGE,"E161"),sQuery(id+"F0.wireOp",EDGE,"E162")])],"isStart":true});
            fillet(context, id + "F2", {"entities" : qUnion([Q0, Q1]), "radius" : 0.5 * mm, "allowEdgeOverflow" : false});
        }
    });
